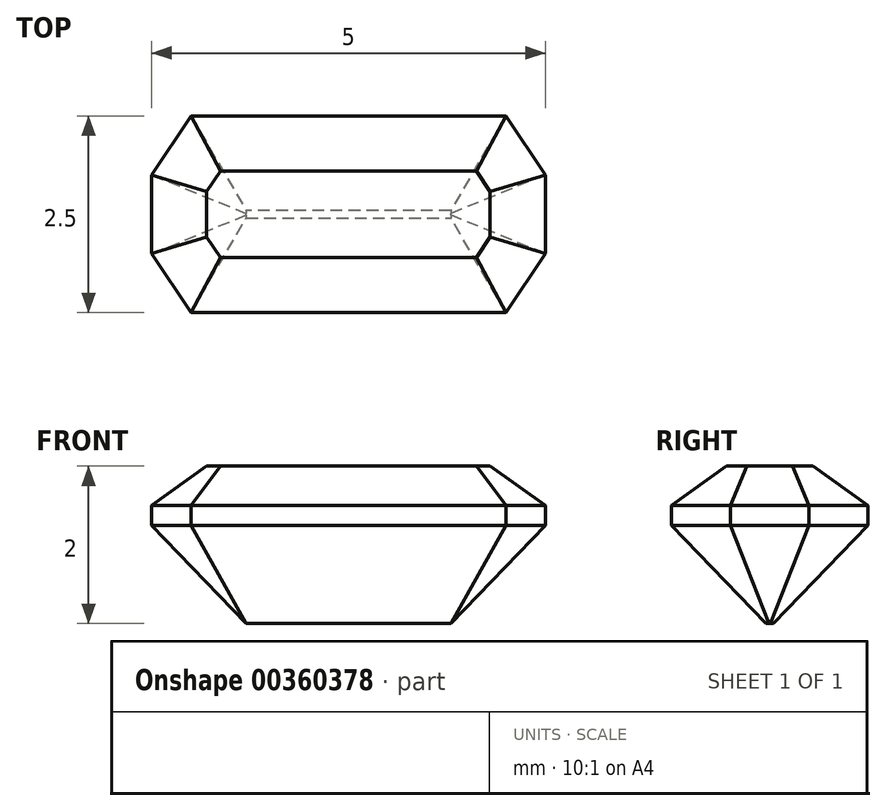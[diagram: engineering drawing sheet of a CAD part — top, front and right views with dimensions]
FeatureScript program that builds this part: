
annotation { "Feature Type Name" : "Feature", "Feature Type Description" : "" }
export const myFeature = defineFeature(function(context is Context, id is Id, definition is map)
    precondition{}
    {
        {
            var Q0;
            Q0=qCreatedBy(makeId("Top.planeOp"),FACE);
            var sketch = newSketch(context, id + "F0", { "sketchPlane" : qUnion([Q0])});
            skLineSegment(sketch, "E0.bottom", {"start": v(2.5, -1.25) * mm, "end": v(-2.5, -1.25) * mm});
            skLineSegment(sketch, "E0.top", {"start": v(2.5, 1.25) * mm, "end": v(-2.5, 1.25) * mm});
            skLineSegment(sketch, "E0.left", {"start": v(2.5, -1.25) * mm, "end": v(2.5, 1.25) * mm});
            skLineSegment(sketch, "E0.right", {"start": v(-2.5, -1.25) * mm, "end": v(-2.5, 1.25) * mm});
            skPoint(sketch, "E0.middle", {"position": v(0, 0) * mm});
            skPoint(sketch, "E1", {"position": v(-2.5, 0) * mm});
            skPoint(sketch, "E2", {"position": v(0, 1.25) * mm});
            skPoint(sketch, "E3", {"position": v(2.5, 0) * mm});
            skPoint(sketch, "E4", {"position": v(0, -1.25) * mm});
            skSolve(sketch);
        }
        {
            var Q0;
            Q0=qCreatedBy(makeId("Top.planeOp"),FACE);
            var sketch = newSketch(context, id + "F1", { "sketchPlane" : qUnion([Q0])});
            skLineSegment(sketch, "E5", {"start": v(0, -1.25) * mm, "end": v(-2, -1.25) * mm});
            skLineSegment(sketch, "E6", {"start": v(-2.5, -0.5) * mm, "end": v(-2, -1.25) * mm});
            skLineSegment(sketch, "E7", {"start": v(81.29, 0) * mm, "end": v(-84.72, 0) * mm, "construction": true});
            skLineSegment(sketch, "E8", {"start": v(0, 46.42) * mm, "end": v(0, -64.87) * mm, "construction": true});
            skPoint(sketch, "E9.0", {"position": v(-2.5, 0) * mm});
            skPoint(sketch, "E10.0", {"position": v(0, 1.25) * mm});
            skPoint(sketch, "E11.0", {"position": v(0, -1.25) * mm});
            skLineSegment(sketch, "E12", {"start": v(-2.5, -0.5) * mm, "end": v(-2.5, 0) * mm});
            skLineSegment(sketch, "E13.MirrorCS", {"start": v(0, 1.25) * mm, "end": v(-2, 1.25) * mm});
            skLineSegment(sketch, "E14.MirrorCS", {"start": v(-2.5, 0.5) * mm, "end": v(-2, 1.25) * mm});
            skLineSegment(sketch, "E15.MirrorCS", {"start": v(-2.5, 0.5) * mm, "end": v(-2.5, 0) * mm});
            skLineSegment(sketch, "E16.MirrorCS", {"start": v(0, 1.25) * mm, "end": v(2, 1.25) * mm});
            skLineSegment(sketch, "E17.MirrorCS", {"start": v(2.5, 0.5) * mm, "end": v(2, 1.25) * mm});
            skLineSegment(sketch, "E18.MirrorCS", {"start": v(2.5, 0.5) * mm, "end": v(2.5, 0) * mm});
            skLineSegment(sketch, "E19.MirrorCS", {"start": v(2.5, -0.5) * mm, "end": v(2.5, 0) * mm});
            skLineSegment(sketch, "E20.MirrorCS", {"start": v(2.5, -0.5) * mm, "end": v(2, -1.25) * mm});
            skLineSegment(sketch, "E21.MirrorCS", {"start": v(0, -1.25) * mm, "end": v(2, -1.25) * mm});
            skSolve(sketch);
        }
        {
            var Q0;
            Q0=qCreatedBy(makeId("Top.planeOp"),FACE);
            cPlane(context, id + "F2", {"entities" : qUnion([Q0]), "cplaneType" : CPlaneType.OFFSET, "offset" : 0.5 * mm, "width" : 152.4 * mm, "height" : 152.4 * mm});
        }
        {
            var Q0;
            Q0=qCreatedBy(id+"F2.planeOp",FACE);
            var sketch = newSketch(context, id + "F3", { "sketchPlane" : qUnion([Q0])});
            skLineSegment(sketch, "E22.0.0", {"start": v(2, -1.25) * mm, "end": v(2.5, -0.5) * mm, "construction": true});
            skLineSegment(sketch, "E22.0.1", {"start": v(2.5, -0.5) * mm, "end": v(2.5, 0) * mm, "construction": true});
            skLineSegment(sketch, "E22.0.2", {"start": v(2.5, 0) * mm, "end": v(2.5, 0.5) * mm, "construction": true});
            skLineSegment(sketch, "E22.0.3", {"start": v(2.5, 0.5) * mm, "end": v(2, 1.25) * mm, "construction": true});
            skLineSegment(sketch, "E22.0.4", {"start": v(2, 1.25) * mm, "end": v(0, 1.25) * mm, "construction": true});
            skLineSegment(sketch, "E22.0.5", {"start": v(0, 1.25) * mm, "end": v(-2, 1.25) * mm, "construction": true});
            skLineSegment(sketch, "E22.0.6", {"start": v(-2, 1.25) * mm, "end": v(-2.5, 0.5) * mm, "construction": true});
            skLineSegment(sketch, "E22.0.7", {"start": v(-2.5, 0.5) * mm, "end": v(-2.5, 0) * mm, "construction": true});
            skLineSegment(sketch, "E22.0.8", {"start": v(-2.5, 0) * mm, "end": v(-2.5, -0.5) * mm, "construction": true});
            skLineSegment(sketch, "E22.0.9", {"start": v(-2.5, -0.5) * mm, "end": v(-2, -1.25) * mm, "construction": true});
            skLineSegment(sketch, "E22.0.10", {"start": v(-2, -1.25) * mm, "end": v(0, -1.25) * mm, "construction": true});
            skLineSegment(sketch, "E22.0.11", {"start": v(0, -1.25) * mm, "end": v(2, -1.25) * mm, "construction": true});
            skLineSegment(sketch, "E23.0", {"start": v(1.63, 0.55) * mm, "end": v(0, 0.55) * mm});
            skLineSegment(sketch, "E23.1", {"start": v(-1.8, -0.29) * mm, "end": v(-1.63, -0.55) * mm});
            skLineSegment(sketch, "E23.2", {"start": v(-1.8, 0) * mm, "end": v(-1.8, -0.29) * mm});
            skLineSegment(sketch, "E23.3", {"start": v(-1.8, 0.29) * mm, "end": v(-1.8, 0) * mm});
            skLineSegment(sketch, "E23.4", {"start": v(-1.63, 0.55) * mm, "end": v(-1.8, 0.29) * mm});
            skLineSegment(sketch, "E23.5", {"start": v(-1.63, -0.55) * mm, "end": v(0, -0.55) * mm});
            skLineSegment(sketch, "E23.6", {"start": v(0, 0.55) * mm, "end": v(-1.63, 0.55) * mm});
            skLineSegment(sketch, "E23.7", {"start": v(0, -0.55) * mm, "end": v(1.63, -0.55) * mm});
            skLineSegment(sketch, "E23.8", {"start": v(1.63, -0.55) * mm, "end": v(1.8, -0.29) * mm});
            skLineSegment(sketch, "E23.9", {"start": v(1.8, -0.29) * mm, "end": v(1.8, 0) * mm});
            skLineSegment(sketch, "E23.10", {"start": v(1.8, 0) * mm, "end": v(1.8, 0.29) * mm});
            skLineSegment(sketch, "E23.11", {"start": v(1.8, 0.29) * mm, "end": v(1.63, 0.55) * mm});
            skSolve(sketch);
        }
        {
            var Q0;
            Q0 = qSketchRegion(id + "F1", true);
            var Q1;
            Q1 = qSketchRegion(id + "F3", true);
            loft(context, id + "F4", {"sheetProfilesArray" : [{ "sheetProfileEntities" : qUnion([Q0]) }, { "sheetProfileEntities" : qUnion([Q1]) }]});
        }
        {
            var Q0;
            Q0=makeQuery(id+"F4.opLoft","CAP_FACE",FACE,{"disambiguationData":[OSD([makeQuery(id+"F1.imprint","IMPRINT",FACE,{"disambiguationData":[TD([[makeQuery(id+"F1.imprint","IMPRINT",EDGE,{"derivedFrom":sQuery(id+"F1.wireOp",EDGE,"E5")}),-1.0]])]})])],"isStart":true});
            extrude(context, id + "F5", {"entities" : qUnion([Q0]), "operationType" : NewBodyOperationType.ADD, "depth" : 0.25 * mm});
        }
        {
            var Q0;
            Q0=makeQuery(id+"F5.opExtrude","CAP_FACE",FACE,{"disambiguationData":[OSD([makeQuery(id+"F1.imprint","IMPRINT",FACE,{"disambiguationData":[TD([[makeQuery(id+"F1.imprint","IMPRINT",EDGE,{"derivedFrom":sQuery(id+"F1.wireOp",EDGE,"E5")}),-1.0]])]})])],"isStart":false});
            var sketch = newSketch(context, id + "F6", { "sketchPlane" : qUnion([Q0])});
            skLineSegment(sketch, "E24.0.0", {"start": v(2, 1.25) * mm, "end": v(2.5, 0.5) * mm});
            skLineSegment(sketch, "E24.0.1", {"start": v(-2, 1.25) * mm, "end": v(2, 1.25) * mm});
            skLineSegment(sketch, "E24.0.2", {"start": v(-2, 1.25) * mm, "end": v(-2.5, 0.5) * mm});
            skLineSegment(sketch, "E24.0.3", {"start": v(-2.5, 0.5) * mm, "end": v(-2.5, -0.5) * mm});
            skLineSegment(sketch, "E24.0.4", {"start": v(-2, -1.25) * mm, "end": v(-2.5, -0.5) * mm});
            skLineSegment(sketch, "E24.0.5", {"start": v(2, -1.25) * mm, "end": v(-2, -1.25) * mm});
            skLineSegment(sketch, "E24.0.6", {"start": v(2, -1.25) * mm, "end": v(2.5, -0.5) * mm});
            skLineSegment(sketch, "E24.0.7", {"start": v(2.5, -0.5) * mm, "end": v(2.5, 0.5) * mm});
            skSolve(sketch);
        }
        {
            var Q0;
            Q0=makeQuery(id+"F5.opExtrude","CAP_FACE",FACE,{"disambiguationData":[OSD([makeQuery(id+"F1.imprint","IMPRINT",FACE,{"disambiguationData":[TD([[makeQuery(id+"F1.imprint","IMPRINT",EDGE,{"derivedFrom":sQuery(id+"F1.wireOp",EDGE,"E5")}),-1.0]])]})])],"isStart":false});
            cPlane(context, id + "F7", {"entities" : qUnion([Q0]), "cplaneType" : CPlaneType.OFFSET, "offset" : 1.25 * mm, "width" : 150 * mm, "height" : 150 * mm});
        }
        {
            var Q0;
            Q0=qCreatedBy(id+"F7.planeOp",FACE);
            var sketch = newSketch(context, id + "F8", { "sketchPlane" : qUnion([Q0])});
            skLineSegment(sketch, "E25.0.0", {"start": v(2, 1.25) * mm, "end": v(2.5, 0.5) * mm, "construction": true});
            skLineSegment(sketch, "E25.0.1", {"start": v(-2, 1.25) * mm, "end": v(2, 1.25) * mm, "construction": true});
            skLineSegment(sketch, "E25.0.2", {"start": v(-2, 1.25) * mm, "end": v(-2.5, 0.5) * mm, "construction": true});
            skLineSegment(sketch, "E25.0.3", {"start": v(-2.5, 0.5) * mm, "end": v(-2.5, -0.5) * mm, "construction": true});
            skLineSegment(sketch, "E25.0.4", {"start": v(-2, -1.25) * mm, "end": v(-2.5, -0.5) * mm, "construction": true});
            skLineSegment(sketch, "E25.0.5", {"start": v(2, -1.25) * mm, "end": v(-2, -1.25) * mm, "construction": true});
            skLineSegment(sketch, "E25.0.6", {"start": v(2, -1.25) * mm, "end": v(2.5, -0.5) * mm, "construction": true});
            skLineSegment(sketch, "E25.0.7", {"start": v(2.5, -0.5) * mm, "end": v(2.5, 0.5) * mm, "construction": true});
            skLineSegment(sketch, "E26.0", {"start": v(-1.3, 0.05) * mm, "end": v(1.3, 0.05) * mm});
            skLineSegment(sketch, "E26.2", {"start": v(1.3, -0.05) * mm, "end": v(-1.3, -0.05) * mm});
            skLineSegment(sketch, "E26.3", {"start": v(1.3, -0.05) * mm, "end": v(1.3, 0) * mm});
            skLineSegment(sketch, "E27", {"start": v(1.3, 0.01) * mm, "end": v(1.3, 0.05) * mm});
            skLineSegment(sketch, "E28", {"start": v(1.3, 0.01) * mm, "end": v(1.3, 0) * mm});
            skLineSegment(sketch, "E29", {"start": v(0, 1.89) * mm, "end": v(0, -1.79) * mm, "construction": true});
            skPoint(sketch, "E29.startSnap0", {"position": v(0, 1.25) * mm});
            skLineSegment(sketch, "E30.MirrorCS", {"start": v(-1.3, 0.01) * mm, "end": v(-1.3, 0.05) * mm});
            skLineSegment(sketch, "E31.MirrorCS", {"start": v(-1.3, 0.01) * mm, "end": v(-1.3, 0) * mm});
            skLineSegment(sketch, "E32.MirrorCS", {"start": v(-1.3, -0.05) * mm, "end": v(-1.3, 0) * mm});
            skSolve(sketch);
        }
        {
            var Q1;
            Q1 = qSketchRegion(id + "F6", true);
            var Q2;
            Q2 = qSketchRegion(id + "F8", true);
            loft(context, id + "F9", {"operationType" : NewBodyOperationType.ADD, "sheetProfilesArray" : [{ "sheetProfileEntities" : qUnion([Q1]) }, { "sheetProfileEntities" : qUnion([Q2]) }]});
        }
    });
